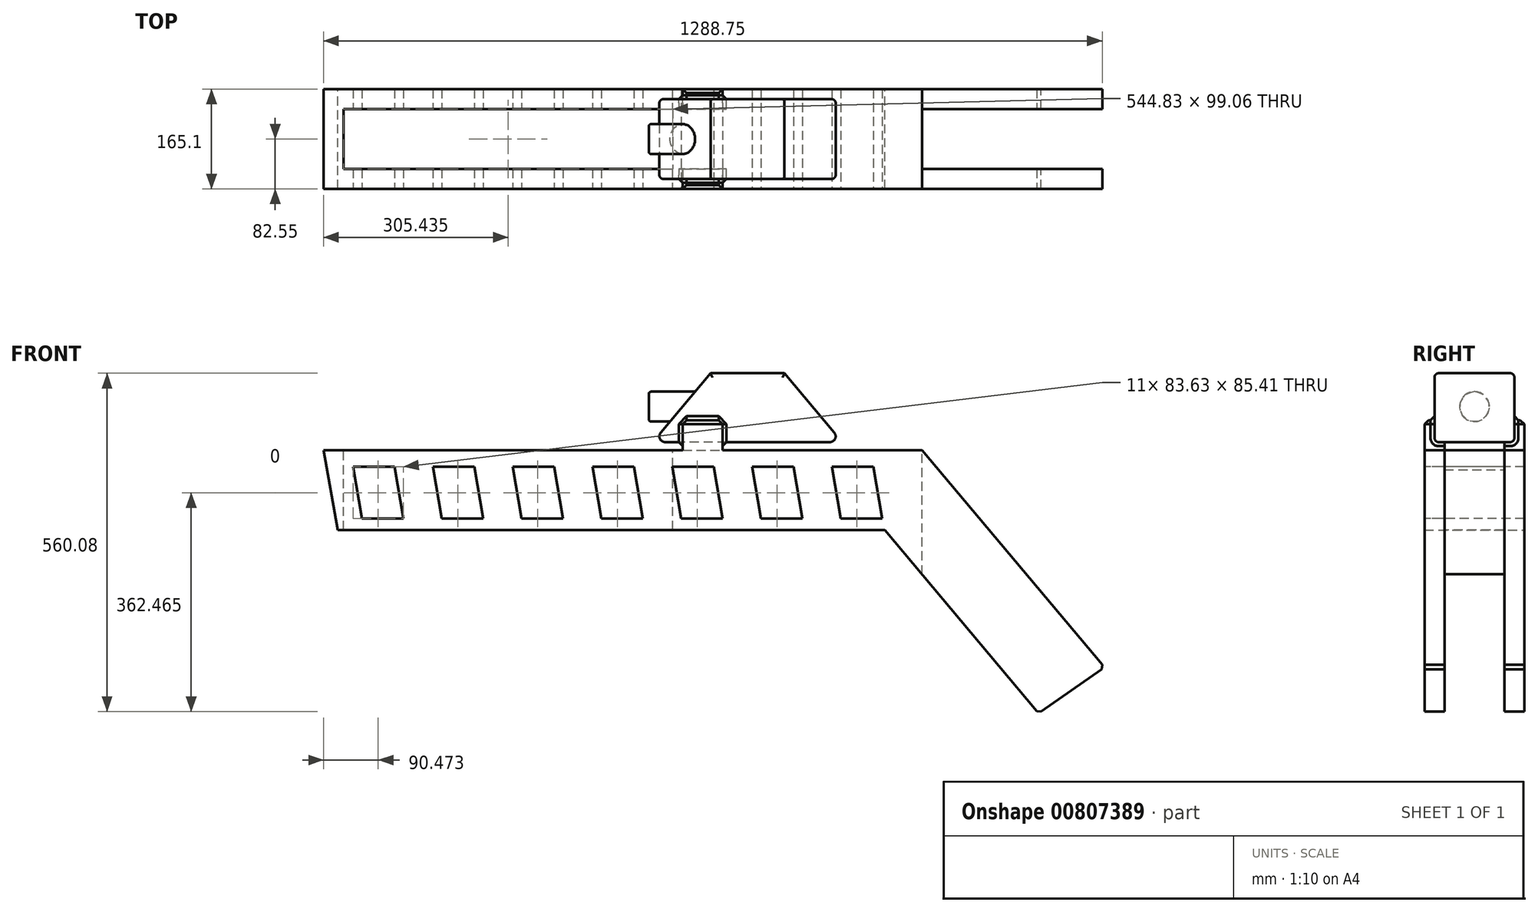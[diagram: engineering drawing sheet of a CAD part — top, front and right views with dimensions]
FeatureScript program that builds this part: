
annotation { "Feature Type Name" : "Feature", "Feature Type Description" : "" }
export const myFeature = defineFeature(function(context is Context, id is Id, definition is map)
    precondition{}
    {
        {
            var Q0;
            Q0=qCreatedBy(makeId("Front.planeOp"),FACE);
            var sketch = newSketch(context, id + "F0", { "sketchPlane" : qUnion([Q0])});
            skLineSegment(sketch, "E0", {"start": v(279.47, -175) * mm, "end": v(47.38, 101.6) * mm});
            skLineSegment(sketch, "E1", {"start": v(47.38, 101.6) * mm, "end": v(-714.62, 101.6) * mm});
            skLineSegment(sketch, "E2", {"start": v(0, 0) * mm, "end": v(195.92, -233.5) * mm});
            skLineSegment(sketch, "E3", {"start": v(195.92, -233.5) * mm, "end": v(279.47, -175) * mm});
            skLineSegment(sketch, "E4", {"start": v(-714.62, 101.6) * mm, "end": v(-696.7, 0) * mm});
            skLineSegment(sketch, "E5", {"start": v(-696.7, 0) * mm, "end": v(0, 0) * mm});
            skSolve(sketch);
        }
        {
            var Q0;
            Q0=makeQuery(id+"F0.imprint","IMPRINT",FACE,{"disambiguationData":[TD([[makeQuery(id+"F0.imprint","IMPRINT",EDGE,{"derivedFrom":sQuery(id+"F0.wireOp",EDGE,"E0")}),1.0]])]});
            extrude(context, id + "F1", {"entities" : qUnion([Q0]), "depth" : 127 * mm, "offsetDistance" : 25.4 * mm});
        }
        {
            var Q0;
            Q0=makeQuery(id+"F1.opExtrude","CAP_FACE",FACE,{"disambiguationData":[OSD([sQuery(id+"F0.wireOp",EDGE,"E0"),sQuery(id+"F0.wireOp",EDGE,"E1"),sQuery(id+"F0.wireOp",EDGE,"E2"),sQuery(id+"F0.wireOp",EDGE,"E3"),sQuery(id+"F0.wireOp",EDGE,"E4"),sQuery(id+"F0.wireOp",EDGE,"E5")])],"isStart":false});
            var sketch = newSketch(context, id + "F2", { "sketchPlane" : qUnion([Q0])});
            skLineSegment(sketch, "E6", {"start": v(-677.2, 80.23) * mm, "end": v(-665.6, 14.53) * mm});
            skLineSegment(sketch, "E7", {"start": v(-665.6, 14.53) * mm, "end": v(-612.86, 14.53) * mm});
            skLineSegment(sketch, "E8", {"start": v(-612.86, 14.53) * mm, "end": v(-624.45, 80.23) * mm});
            skLineSegment(sketch, "E9", {"start": v(-624.45, 80.23) * mm, "end": v(-677.2, 80.23) * mm});
            skLineSegment(sketch, "E10.1.0.0", {"start": v(-564, 14.53) * mm, "end": v(-511.26, 14.53) * mm});
            skLineSegment(sketch, "E10.1.0.1", {"start": v(-511.26, 14.53) * mm, "end": v(-522.85, 80.23) * mm});
            skLineSegment(sketch, "E10.1.0.2", {"start": v(-522.85, 80.23) * mm, "end": v(-575.6, 80.23) * mm});
            skLineSegment(sketch, "E10.1.0.3", {"start": v(-575.6, 80.23) * mm, "end": v(-564, 14.53) * mm});
            skLineSegment(sketch, "E10.2.0.0", {"start": v(-462.4, 14.53) * mm, "end": v(-409.66, 14.53) * mm});
            skLineSegment(sketch, "E10.2.0.1", {"start": v(-409.66, 14.53) * mm, "end": v(-421.25, 80.23) * mm});
            skLineSegment(sketch, "E10.2.0.2", {"start": v(-421.25, 80.23) * mm, "end": v(-474, 80.23) * mm});
            skLineSegment(sketch, "E10.2.0.3", {"start": v(-474, 80.23) * mm, "end": v(-462.4, 14.53) * mm});
            skLineSegment(sketch, "E10.3.0.0", {"start": v(-360.8, 14.53) * mm, "end": v(-308.06, 14.53) * mm});
            skLineSegment(sketch, "E10.3.0.1", {"start": v(-308.06, 14.53) * mm, "end": v(-319.65, 80.23) * mm});
            skLineSegment(sketch, "E10.3.0.2", {"start": v(-319.65, 80.23) * mm, "end": v(-372.4, 80.23) * mm});
            skLineSegment(sketch, "E10.3.0.3", {"start": v(-372.4, 80.23) * mm, "end": v(-360.8, 14.53) * mm});
            skLineSegment(sketch, "E10.4.0.0", {"start": v(-259.2, 14.53) * mm, "end": v(-206.46, 14.53) * mm});
            skLineSegment(sketch, "E10.4.0.1", {"start": v(-206.46, 14.53) * mm, "end": v(-218.05, 80.23) * mm});
            skLineSegment(sketch, "E10.4.0.2", {"start": v(-218.05, 80.23) * mm, "end": v(-270.8, 80.23) * mm});
            skLineSegment(sketch, "E10.4.0.3", {"start": v(-270.8, 80.23) * mm, "end": v(-259.2, 14.53) * mm});
            skLineSegment(sketch, "E10.5.0.0", {"start": v(-157.6, 14.53) * mm, "end": v(-104.86, 14.53) * mm});
            skLineSegment(sketch, "E10.5.0.1", {"start": v(-104.86, 14.53) * mm, "end": v(-116.45, 80.23) * mm});
            skLineSegment(sketch, "E10.5.0.2", {"start": v(-116.45, 80.23) * mm, "end": v(-169.2, 80.23) * mm});
            skLineSegment(sketch, "E10.5.0.3", {"start": v(-169.2, 80.23) * mm, "end": v(-157.6, 14.53) * mm});
            skLineSegment(sketch, "E10.6.0.0", {"start": v(-56, 14.53) * mm, "end": v(-3.26, 14.53) * mm});
            skLineSegment(sketch, "E10.6.0.1", {"start": v(-3.26, 14.53) * mm, "end": v(-14.85, 80.23) * mm});
            skLineSegment(sketch, "E10.6.0.2", {"start": v(-14.85, 80.23) * mm, "end": v(-67.6, 80.23) * mm});
            skLineSegment(sketch, "E10.6.0.3", {"start": v(-67.6, 80.23) * mm, "end": v(-56, 14.53) * mm});
            skLineSegment(sketch, "E10.direction1", {"start": v(-665.6, 14.53) * mm, "end": v(-564, 14.53) * mm, "construction": true});
            skSolve(sketch);
        }
        {
            var Q0;
            Q0=makeQuery(id+"F2.imprint","IMPRINT",FACE,{"disambiguationData":[TD([[makeQuery(id+"F2.imprint","IMPRINT",EDGE,{"derivedFrom":sQuery(id+"F2.wireOp",EDGE,"E6")}),1.0]])]});
            var Q1;
            Q1=makeQuery(id+"F2.imprint","IMPRINT",FACE,{"disambiguationData":[TD([[makeQuery(id+"F2.imprint","IMPRINT",EDGE,{"derivedFrom":sQuery(id+"F2.wireOp",EDGE,"E10.1.0.0")}),1.0]])]});
            var Q2;
            Q2=makeQuery(id+"F2.imprint","IMPRINT",FACE,{"disambiguationData":[TD([[makeQuery(id+"F2.imprint","IMPRINT",EDGE,{"derivedFrom":sQuery(id+"F2.wireOp",EDGE,"E10.2.0.0")}),1.0]])]});
            var Q3;
            Q3=makeQuery(id+"F2.imprint","IMPRINT",FACE,{"disambiguationData":[TD([[makeQuery(id+"F2.imprint","IMPRINT",EDGE,{"derivedFrom":sQuery(id+"F2.wireOp",EDGE,"E10.3.0.0")}),1.0]])]});
            var Q4;
            Q4=makeQuery(id+"F2.imprint","IMPRINT",FACE,{"disambiguationData":[TD([[makeQuery(id+"F2.imprint","IMPRINT",EDGE,{"derivedFrom":sQuery(id+"F2.wireOp",EDGE,"E10.4.0.0")}),1.0]])]});
            var Q5;
            Q5=makeQuery(id+"F2.imprint","IMPRINT",FACE,{"disambiguationData":[TD([[makeQuery(id+"F2.imprint","IMPRINT",EDGE,{"derivedFrom":sQuery(id+"F2.wireOp",EDGE,"E10.5.0.0")}),1.0]])]});
            var Q6;
            Q6=makeQuery(id+"F2.imprint","IMPRINT",FACE,{"disambiguationData":[TD([[makeQuery(id+"F2.imprint","IMPRINT",EDGE,{"derivedFrom":sQuery(id+"F2.wireOp",EDGE,"E10.6.0.0")}),1.0]])]});
            var Q7;
            Q7=makeQuery(id+"F1.opExtrude","CAP_FACE",FACE,{"disambiguationData":[OSD([sQuery(id+"F0.wireOp",EDGE,"E0"),sQuery(id+"F0.wireOp",EDGE,"E1"),sQuery(id+"F0.wireOp",EDGE,"E2"),sQuery(id+"F0.wireOp",EDGE,"E3"),sQuery(id+"F0.wireOp",EDGE,"E4"),sQuery(id+"F0.wireOp",EDGE,"E5")])],"isStart":true});
            extrude(context, id + "F3", {"entities" : qUnion([Q0, Q1, Q2, Q3, Q4, Q5, Q6]), "operationType" : NewBodyOperationType.REMOVE, "endBound" : BoundingType.UP_TO_SURFACE, "oppositeDirection" : true, "depth" : 25.4 * mm, "endBoundEntityFace" : qUnion([Q7]), "offsetDistance" : 25.4 * mm});
        }
        {
            var Q0;
            Q0=makeQuery(id+"F1.opExtrude","SWEPT_FACE",FACE,{"disambiguationData":[OSD([sQuery(id+"F0.wireOp",EDGE,"E1")])]});
            var sketch = newSketch(context, id + "F4", { "sketchPlane" : qUnion([Q0])});
            skLineSegment(sketch, "E11.bottom", {"start": v(-79.62, -25.4) * mm, "end": v(-117.72, -25.4) * mm});
            skLineSegment(sketch, "E11.top", {"start": v(-79.62, -101.6) * mm, "end": v(-117.72, -101.6) * mm});
            skLineSegment(sketch, "E11.left", {"start": v(-79.62, -25.4) * mm, "end": v(-79.62, -101.6) * mm});
            skLineSegment(sketch, "E11.right", {"start": v(-117.72, -25.4) * mm, "end": v(-117.72, -101.6) * mm});
            skLineSegment(sketch, "E12.bottom", {"start": v(-232.02, -25.4) * mm, "end": v(-270.12, -25.4) * mm});
            skLineSegment(sketch, "E12.top", {"start": v(-232.02, -101.6) * mm, "end": v(-270.12, -101.6) * mm});
            skLineSegment(sketch, "E12.left", {"start": v(-232.02, -25.4) * mm, "end": v(-232.02, -101.6) * mm});
            skLineSegment(sketch, "E12.right", {"start": v(-270.12, -25.4) * mm, "end": v(-270.12, -101.6) * mm});
            skSolve(sketch);
        }
        {
            var Q0;
            Q0=makeQuery(id+"F4.imprint","IMPRINT",FACE,{"disambiguationData":[TD([[makeQuery(id+"F4.imprint","IMPRINT",EDGE,{"derivedFrom":sQuery(id+"F4.wireOp",EDGE,"E12.bottom")}),1.0]])]});
            var Q1;
            Q1=makeQuery(id+"F4.imprint","IMPRINT",FACE,{"disambiguationData":[TD([[makeQuery(id+"F4.imprint","IMPRINT",EDGE,{"derivedFrom":sQuery(id+"F4.wireOp",EDGE,"E11.bottom")}),1.0]])]});
            extrude(context, id + "F5", {"entities" : qUnion([Q0, Q1]), "operationType" : NewBodyOperationType.ADD, "depth" : 10.16 * mm, "offsetDistance" : 25.4 * mm});
        }
        {
            var Q0;
            Q0=makeQuery(id+"F5.opExtrude","CAP_FACE",FACE,{"disambiguationData":[OSD([sQuery(id+"F4.wireOp",EDGE,"E12.bottom"),sQuery(id+"F4.wireOp",EDGE,"E12.top"),sQuery(id+"F4.wireOp",EDGE,"E12.left"),sQuery(id+"F4.wireOp",EDGE,"E12.right")])],"isStart":false});
            var sketch = newSketch(context, id + "F6", { "sketchPlane" : qUnion([Q0])});
            skLineSegment(sketch, "E13.bottom", {"start": v(-295.52, -12.7) * mm, "end": v(-54.22, -12.7) * mm});
            skLineSegment(sketch, "E13.top", {"start": v(-295.52, -114.3) * mm, "end": v(-54.22, -114.3) * mm});
            skLineSegment(sketch, "E13.left", {"start": v(-295.52, -12.7) * mm, "end": v(-295.52, -114.3) * mm});
            skLineSegment(sketch, "E13.right", {"start": v(-54.22, -12.7) * mm, "end": v(-54.22, -114.3) * mm});
            skSolve(sketch);
        }
        {
            var Q0;
            Q0=makeQuery(id+"F6.imprint","IMPRINT",FACE,{"disambiguationData":[TD([[makeQuery(id+"F6.imprint","IMPRINT",EDGE,{"derivedFrom":sQuery(id+"F6.wireOp",EDGE,"E13.bottom")}),-1.0]])]});
            var Q1;
            Q1=makeQuery(id+"F6.imprint","IMPRINT",FACE,{"disambiguationData":[TD([[makeQuery(id+"F6.imprint","IMPRINT",EDGE,{"derivedFrom":makeQuery(id+"F5.opExtrude","CAP_EDGE",EDGE,{"disambiguationData":[OSD([sQuery(id+"F4.wireOp",EDGE,"E12.bottom")])],"isStart":false})}),1.0]])]});
            extrude(context, id + "F7", {"entities" : qUnion([Q0, Q1]), "operationType" : NewBodyOperationType.ADD, "depth" : 87.63 * mm, "offsetDistance" : 25.4 * mm});
        }
        {
            var Q0;
            Q0=makeQuery(id+"F7.opExtrude","SWEPT_FACE",FACE,{"disambiguationData":[OSD([sQuery(id+"F6.wireOp",EDGE,"E13.top")])]});
            var sketch = newSketch(context, id + "F8", { "sketchPlane" : qUnion([Q0])});
            skLineSegment(sketch, "E14", {"start": v(-295.52, 111.76) * mm, "end": v(-222, 199.39) * mm});
            skLineSegment(sketch, "E15", {"start": v(-54.22, 111.76) * mm, "end": v(-127.75, 199.39) * mm});
            skSolve(sketch);
        }
        {
            var Q0;
            {var subQ0=sQuery(id+"F8.wireOp",EDGE,"E14");Q0=makeQuery(id+"F8.imprint","IMPRINT",FACE,{"disambiguationData":[TD([[makeQuery(id+"F8.imprint","IMPRINT",EDGE,{"derivedFrom":subQ0}),1.0]])]});}
            var Q1;
            {var subQ0=sQuery(id+"F8.wireOp",EDGE,"E15");Q1=makeQuery(id+"F8.imprint","IMPRINT",FACE,{"disambiguationData":[TD([[makeQuery(id+"F8.imprint","IMPRINT",EDGE,{"derivedFrom":subQ0}),-1.0]])]});}
            var Q2;
            Q2=makeQuery(id+"F7.opExtrude","SWEPT_FACE",FACE,{"disambiguationData":[OSD([sQuery(id+"F6.wireOp",EDGE,"E13.bottom")])]});
            extrude(context, id + "F9", {"entities" : qUnion([Q0, Q1]), "operationType" : NewBodyOperationType.REMOVE, "endBound" : BoundingType.UP_TO_SURFACE, "oppositeDirection" : true, "depth" : 25.4 * mm, "endBoundEntityFace" : qUnion([Q2]), "offsetDistance" : 25.4 * mm});
        }
        {
            var Q0;
            {var subQ0=sQuery(id+"F6.wireOp",EDGE,"E13.right");Q0=makeQuery(id+"F9.boolean.opBoolean","MERGE",EDGE,{"derivedFrom":[makeQuery(id+"F7.opExtrude","CAP_EDGE",EDGE,{"disambiguationData":[OSD([subQ0])],"isStart":true})],"fromTools":[makeQuery(id+"F9.opExtrude","SWEPT_EDGE",EDGE,{"disambiguationData":[OSD([sQuery(id+"F6.wireOp",EDGE,"E13.top"),subQ0,sQuery(id+"F8.wireOp",EDGE,"E15")])]})]});}
            var Q1;
            {var subQ0=sQuery(id+"F6.wireOp",EDGE,"E13.left");Q1=makeQuery(id+"F9.boolean.opBoolean","MERGE",EDGE,{"derivedFrom":[makeQuery(id+"F7.opExtrude","CAP_EDGE",EDGE,{"disambiguationData":[OSD([subQ0])],"isStart":true})],"fromTools":[makeQuery(id+"F9.opExtrude","SWEPT_EDGE",EDGE,{"disambiguationData":[OSD([sQuery(id+"F6.wireOp",EDGE,"E13.top"),subQ0,sQuery(id+"F8.wireOp",EDGE,"E14")])]})]});}
            var Q2;
            Q2=makeQuery(id+"F9.boolean.opBoolean","COPY",EDGE,{"derivedFrom":makeQuery(id+"F9.opExtrude","SWEPT_EDGE",EDGE,{"disambiguationData":[OSD([sQuery(id+"F6.wireOp",EDGE,"E13.top"),sQuery(id+"F8.wireOp",EDGE,"E14")])]})});
            var Q3;
            Q3=makeQuery(id+"F9.boolean.opBoolean","COPY",EDGE,{"derivedFrom":makeQuery(id+"F9.opExtrude","SWEPT_EDGE",EDGE,{"disambiguationData":[OSD([sQuery(id+"F6.wireOp",EDGE,"E13.top"),sQuery(id+"F8.wireOp",EDGE,"E15")])]})});
            fillet(context, id + "F10", {"entities" : qUnion([Q0, Q1, Q2, Q3]), "tangentPropagation" : true, "radius" : 7.37 * mm, "defaultsChanged" : true, "vertexSettings" : [], "allowEdgeOverflow" : false});
        }
        {
            var Q0;
            Q0=makeQuery(id+"F7.opExtrude","SWEPT_FACE",FACE,{"disambiguationData":[OSD([sQuery(id+"F6.wireOp",EDGE,"E13.bottom")])]});
            var Q1;
            Q1=makeQuery(id+"F7.opExtrude","SWEPT_FACE",FACE,{"disambiguationData":[OSD([sQuery(id+"F6.wireOp",EDGE,"E13.top")])]});
            fillet(context, id + "F11", {"entities" : qUnion([Q0, Q1]), "tangentPropagation" : true, "radius" : 5.08 * mm, "defaultsChanged" : false, "vertexSettings" : [], "allowEdgeOverflow" : false});
        }
        {
            var Q0;
            Q0=makeQuery(id+"F5.opExtrude","SWEPT_FACE",FACE,{"disambiguationData":[OSD([sQuery(id+"F4.wireOp",EDGE,"E12.right")])]});
            var sketch = newSketch(context, id + "F12", { "sketchPlane" : qUnion([Q0])});
            skCircle(sketch, "E16", {"center": v(63.5, 156.89) * mm, "radius": 19.05 * mm});
            skSolve(sketch);
        }
        {
            var Q0;
            Q0=makeQuery(id+"F12.imprint","IMPRINT",FACE,{"disambiguationData":[TD([[makeQuery(id+"F12.imprint","IMPRINT",EDGE,{"derivedFrom":sQuery(id+"F12.wireOp",EDGE,"E16")}),1.0]])]});
            extrude(context, id + "F13", {"entities" : qUnion([Q0]), "operationType" : NewBodyOperationType.ADD, "depth" : 30.48 * mm, "offsetDistance" : 25.4 * mm, "hasSecondDirection" : true, "secondDirectionOppositeDirection" : true, "secondDirectionDepth" : 50.8 * mm});
        }
        {
            var Q0;
            Q0=makeQuery(id+"F13.opExtrude","CAP_EDGE",EDGE,{"disambiguationData":[OSD([sQuery(id+"F12.wireOp",EDGE,"E16")])],"isStart":false});
            fillet(context, id + "F14", {"entities" : qUnion([Q0]), "tangentPropagation" : true, "radius" : 3.07 * mm, "defaultsChanged" : false, "vertexSettings" : [], "allowEdgeOverflow" : false});
        }
        {
            var Q0;
            Q0=makeQuery(id+"F1.opExtrude","SWEPT_FACE",FACE,{"disambiguationData":[OSD([sQuery(id+"F0.wireOp",EDGE,"E1")])]});
            var sketch = newSketch(context, id + "F15", { "sketchPlane" : qUnion([Q0])});
            skLineSegment(sketch, "E17.bottom", {"start": v(-689.22, -25.4) * mm, "end": v(279.47, -25.4) * mm});
            skLineSegment(sketch, "E17.top", {"start": v(-689.22, -101.6) * mm, "end": v(279.47, -101.6) * mm});
            skLineSegment(sketch, "E17.left", {"start": v(-689.22, -25.4) * mm, "end": v(-689.22, -101.6) * mm});
            skLineSegment(sketch, "E17.right", {"start": v(279.47, -25.4) * mm, "end": v(279.47, -101.6) * mm});
            skSolve(sketch);
        }
        {
            var Q0;
            Q0=makeQuery(id+"F5.opExtrude","SWEPT_FACE",FACE,{"disambiguationData":[OSD([sQuery(id+"F4.wireOp",EDGE,"E12.right")])]});
            var Q1;
            Q1=makeQuery(id+"F5.opExtrude","SWEPT_FACE",FACE,{"disambiguationData":[OSD([sQuery(id+"F4.wireOp",EDGE,"E11.left")])]});
            extrude(context, id + "F16", {"entities" : qUnion([Q0]), "operationType" : NewBodyOperationType.REMOVE, "endBound" : BoundingType.UP_TO_SURFACE, "oppositeDirection" : true, "depth" : 25.4 * mm, "endBoundEntityFace" : qUnion([Q1]), "offsetDistance" : 25.4 * mm});
        }
        {
            var Q0;
            {var subQ2=sQuery(id+"F15.wireOp",EDGE,"E17.left");Q0=makeQuery(id+"F15.imprint","IMPRINT",FACE,{"disambiguationData":[TD([[makeQuery(id+"F15.imprint","IMPRINT",EDGE,{"derivedFrom":subQ2}),1.0]])]});}
            var Q1;
            {var subQ1=makeQuery(id+"F5.opExtrude","CAP_EDGE",EDGE,{"disambiguationData":[OSD([sQuery(id+"F4.wireOp",EDGE,"E12.left")])],"isStart":true});Q1=makeQuery(id+"F15.imprint","IMPRINT",FACE,{"disambiguationData":[TD([[makeQuery(id+"F15.imprint","IMPRINT",EDGE,{"derivedFrom":subQ1}),-1.0]])]});}
            var Q2;
            {var subQ1=makeQuery(id+"F5.opExtrude","CAP_EDGE",EDGE,{"disambiguationData":[OSD([sQuery(id+"F4.wireOp",EDGE,"E11.right")])],"isStart":true});Q2=makeQuery(id+"F15.imprint","IMPRINT",FACE,{"disambiguationData":[TD([[makeQuery(id+"F15.imprint","IMPRINT",EDGE,{"derivedFrom":subQ1}),-1.0]])]});}
            var Q3;
            {var subQ1=makeQuery(id+"F5.opExtrude","CAP_EDGE",EDGE,{"disambiguationData":[OSD([sQuery(id+"F4.wireOp",EDGE,"E11.left")])],"isStart":true});Q3=makeQuery(id+"F15.imprint","IMPRINT",FACE,{"disambiguationData":[TD([[makeQuery(id+"F15.imprint","IMPRINT",EDGE,{"derivedFrom":subQ1}),1.0]])]});}
            var Q4;
            {var subQ1=makeQuery(id+"F5.opExtrude","CAP_EDGE",EDGE,{"disambiguationData":[OSD([sQuery(id+"F4.wireOp",EDGE,"E11.left")])],"isStart":true});Q4=makeQuery(id+"F15.imprint","IMPRINT",FACE,{"disambiguationData":[TD([[makeQuery(id+"F15.imprint","IMPRINT",EDGE,{"derivedFrom":subQ1}),-1.0]])]});}
            var Q5;
            {var subQ0=sQuery(id+"F15.wireOp",EDGE,"E17.right");Q5=makeQuery(id+"F15.imprint","IMPRINT",FACE,{"disambiguationData":[TD([[makeQuery(id+"F15.imprint","IMPRINT",EDGE,{"derivedFrom":subQ0}),-1.0]])]});}
            var Q6;
            Q6=makeQuery(id+"F1.opExtrude","SWEPT_FACE",FACE,{"disambiguationData":[OSD([sQuery(id+"F0.wireOp",EDGE,"E5")])]});
            extrude(context, id + "F17", {"entities" : qUnion([Q0, Q1, Q2, Q3, Q4, Q5]), "operationType" : NewBodyOperationType.REMOVE, "oppositeDirection" : true, "depth" : 477.52 * mm, "endBoundEntityFace" : qUnion([Q6]), "offsetDistance" : 25.4 * mm});
        }
        {
            var Q0;
            {var subQ0=sQuery(id+"F4.wireOp",EDGE,"E12.right");Q0=makeQuery(id+"F16.boolean.opBoolean","MERGE",FACE,{"derivedFrom":[makeQuery(id+"F1.opExtrude","SWEPT_FACE",FACE,{"disambiguationData":[OSD([sQuery(id+"F0.wireOp",EDGE,"E1")])]})],"fromTools":[makeQuery(id+"F16.opExtrude","SWEPT_FACE",FACE,{"disambiguationData":[OSD([subQ0]),TDD([makeQuery(id+"F5.opExtrude","CAP_EDGE",EDGE,{"disambiguationData":[OSD([subQ0])],"isStart":true})])]})]});}
            var sketch = newSketch(context, id + "F18", { "sketchPlane" : qUnion([Q0])});
            skLineSegment(sketch, "E18.bottom", {"start": v(-257.42, -101.6) * mm, "end": v(-206.62, -101.6) * mm});
            skLineSegment(sketch, "E18.top", {"start": v(-257.42, -127) * mm, "end": v(-206.62, -127) * mm});
            skLineSegment(sketch, "E18.left", {"start": v(-257.42, -101.6) * mm, "end": v(-257.42, -127) * mm});
            skLineSegment(sketch, "E18.right", {"start": v(-206.62, -101.6) * mm, "end": v(-206.62, -127) * mm});
            skLineSegment(sketch, "E19.bottom", {"start": v(-257.42, 0) * mm, "end": v(-206.62, 0) * mm});
            skLineSegment(sketch, "E19.top", {"start": v(-257.42, -25.4) * mm, "end": v(-206.62, -25.4) * mm});
            skLineSegment(sketch, "E19.left", {"start": v(-257.42, 0) * mm, "end": v(-257.42, -25.4) * mm});
            skLineSegment(sketch, "E19.right", {"start": v(-206.62, 0) * mm, "end": v(-206.62, -25.4) * mm});
            skSolve(sketch);
        }
        {
            var Q0;
            Q0=makeQuery(id+"F18.imprint","IMPRINT",FACE,{"disambiguationData":[TD([[makeQuery(id+"F18.imprint","IMPRINT",EDGE,{"derivedFrom":sQuery(id+"F18.wireOp",EDGE,"E19.bottom")}),1.0]])]});
            var Q1;
            Q1=makeQuery(id+"F18.imprint","IMPRINT",FACE,{"disambiguationData":[TD([[makeQuery(id+"F18.imprint","IMPRINT",EDGE,{"derivedFrom":sQuery(id+"F18.wireOp",EDGE,"E18.bottom")}),-1.0]])]});
            extrude(context, id + "F19", {"entities" : qUnion([Q0, Q1]), "operationType" : NewBodyOperationType.ADD, "depth" : 38.1 * mm, "offsetDistance" : 25.4 * mm});
        }
        {
            var Q0;
            Q0=makeQuery(id+"F19.opExtrude","CAP_EDGE",EDGE,{"disambiguationData":[OSD([sQuery(id+"F18.wireOp",EDGE,"E18.top")])],"isStart":false});
            var Q1;
            Q1=makeQuery(id+"F19.opExtrude","CAP_EDGE",EDGE,{"disambiguationData":[OSD([sQuery(id+"F18.wireOp",EDGE,"E19.bottom")])],"isStart":false});
            var Q2;
            Q2=makeQuery(id+"F19.opExtrude","CAP_FACE",FACE,{"disambiguationData":[OSD([sQuery(id+"F18.wireOp",EDGE,"E19.bottom"),sQuery(id+"F18.wireOp",EDGE,"E19.top"),sQuery(id+"F18.wireOp",EDGE,"E19.left"),sQuery(id+"F18.wireOp",EDGE,"E19.right")])],"isStart":false});
            var Q3;
            Q3=makeQuery(id+"F19.opExtrude","CAP_FACE",FACE,{"disambiguationData":[OSD([sQuery(id+"F18.wireOp",EDGE,"E18.bottom"),sQuery(id+"F18.wireOp",EDGE,"E18.top"),sQuery(id+"F18.wireOp",EDGE,"E18.left"),sQuery(id+"F18.wireOp",EDGE,"E18.right")])],"isStart":false});
            chamfer(context, id + "F20", {"entities" : qUnion([Q0, Q1, Q2, Q3]), "width" : 5.08 * mm, "tangentPropagation" : true});
        }
        {
            var Q0;
            Q0=makeQuery(id+"F16.boolean.opBoolean","SPLIT",BODY,{"disambiguationData":[OD(0.0)],"derivedFrom":makeQuery(id+"F1.opExtrude","SWEPT_BODY",BODY,{"disambiguationData":[OSD([sQuery(id+"F0.wireOp",EDGE,"E0"),sQuery(id+"F0.wireOp",EDGE,"E1"),sQuery(id+"F0.wireOp",EDGE,"E2"),sQuery(id+"F0.wireOp",EDGE,"E3"),sQuery(id+"F0.wireOp",EDGE,"E4"),sQuery(id+"F0.wireOp",EDGE,"E5")])]})});
            var Q1;
            Q1=qCreatedBy(makeId("Origin.pointOp"),VERTEX);
            transform(context, id + "F21", {"entities" : qUnion([Q0]), "transformType" : TransformType.SCALE_UNIFORMLY, "scale" : 1.3, "scalePoint" : qUnion([Q1]), "makeCopy" : false});
        }
        {
            var Q0;
            {var subQ0=sQuery(id+"F0.wireOp",EDGE,"E3");var subQ1=sQuery(id+"F0.wireOp",EDGE,"E2");Q0=makeQuery(id+"F17.boolean.opBoolean","SPLIT",EDGE,{"disambiguationData":[TD([makeQuery(id+"F17.opExtrude","SWEPT_FACE",FACE,{"disambiguationData":[OSD([sQuery(id+"F15.wireOp",EDGE,"E17.top")])]})])],"derivedFrom":makeQuery(id+"F1.opExtrude","SWEPT_EDGE",EDGE,{"disambiguationData":[OSD([subQ1,subQ0])]})});}
            var Q1;
            {var subQ0=sQuery(id+"F0.wireOp",EDGE,"E3");var subQ1=sQuery(id+"F0.wireOp",EDGE,"E2");Q1=makeQuery(id+"F17.boolean.opBoolean","SPLIT",EDGE,{"disambiguationData":[TD([makeQuery(id+"F17.opExtrude","SWEPT_FACE",FACE,{"disambiguationData":[OSD([sQuery(id+"F15.wireOp",EDGE,"E17.bottom")])]})])],"derivedFrom":makeQuery(id+"F1.opExtrude","SWEPT_EDGE",EDGE,{"disambiguationData":[OSD([subQ1,subQ0])]})});}
            var Q2;
            {var subQ0=sQuery(id+"F0.wireOp",EDGE,"E0");var subQ1=sQuery(id+"F0.wireOp",EDGE,"E3");Q2=makeQuery(id+"F17.boolean.opBoolean","SPLIT",EDGE,{"disambiguationData":[TD([makeQuery(id+"F17.opExtrude","SWEPT_FACE",FACE,{"disambiguationData":[OSD([sQuery(id+"F15.wireOp",EDGE,"E17.top")])]})])],"derivedFrom":makeQuery(id+"F1.opExtrude","SWEPT_EDGE",EDGE,{"disambiguationData":[OSD([subQ0,subQ1])]})});}
            var Q3;
            {var subQ0=sQuery(id+"F0.wireOp",EDGE,"E0");var subQ1=sQuery(id+"F0.wireOp",EDGE,"E3");Q3=makeQuery(id+"F17.boolean.opBoolean","SPLIT",EDGE,{"disambiguationData":[TD([makeQuery(id+"F17.opExtrude","SWEPT_FACE",FACE,{"disambiguationData":[OSD([sQuery(id+"F15.wireOp",EDGE,"E17.bottom")])]})])],"derivedFrom":makeQuery(id+"F1.opExtrude","SWEPT_EDGE",EDGE,{"disambiguationData":[OSD([subQ0,subQ1])]})});}
            chamfer(context, id + "F22", {"entities" : qUnion([Q0, Q1, Q2, Q3]), "width" : 5.08 * mm, "tangentPropagation" : true});
        }
    });
